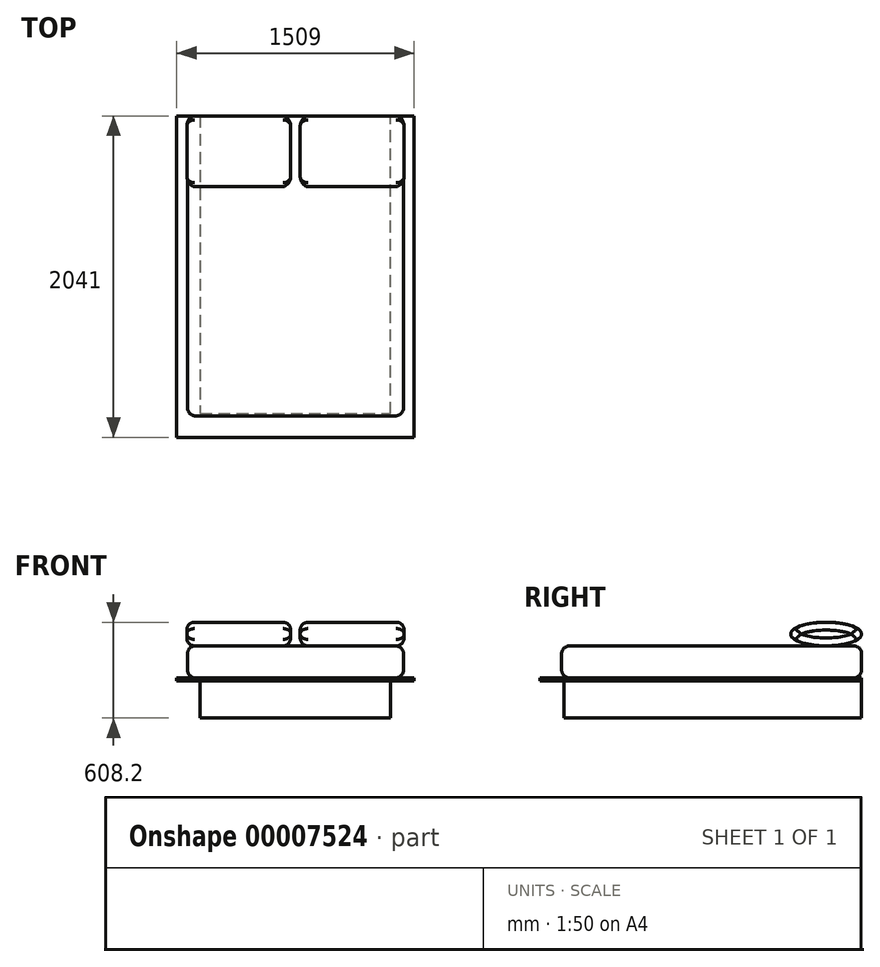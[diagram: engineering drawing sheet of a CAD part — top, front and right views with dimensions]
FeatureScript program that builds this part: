
annotation { "Feature Type Name" : "Feature", "Feature Type Description" : "" }
export const myFeature = defineFeature(function(context is Context, id is Id, definition is map)
    precondition{}
    {
        {
            var Q0;
            Q0=qCreatedBy(makeId("Top.planeOp"),FACE);
            var sketch = newSketch(context, id + "F0", { "sketchPlane" : qUnion([Q0])});
            skLineSegment(sketch, "E0", {"start": v(0, 1020.5) * mm, "end": v(0, -1020.5) * mm, "construction": true});
            skLineSegment(sketch, "E1", {"start": v(-754.5, 0) * mm, "end": v(754.5, 0) * mm, "construction": true});
            skLineSegment(sketch, "E2.bottom", {"start": v(-754.5, 1020.5) * mm, "end": v(754.5, 1020.5) * mm});
            skLineSegment(sketch, "E2.top", {"start": v(-754.5, -1020.5) * mm, "end": v(754.5, -1020.5) * mm});
            skLineSegment(sketch, "E2.left", {"start": v(-754.5, 1020.5) * mm, "end": v(-754.5, -1020.5) * mm});
            skLineSegment(sketch, "E2.right", {"start": v(754.5, 1020.5) * mm, "end": v(754.5, -1020.5) * mm});
            skSolve(sketch);
        }
        {
            var Q0;
            Q0=makeQuery(id+"F0.imprint","IMPRINT",FACE,{"disambiguationData":[TD([[makeQuery(id+"F0.imprint","IMPRINT",EDGE,{"derivedFrom":sQuery(id+"F0.wireOp",EDGE,"E2.bottom")}),-1.0]])]});
            extrude(context, id + "F1", {"entities" : qUnion([Q0]), "oppositeDirection" : true, "depth" : 19 * mm});
        }
        {
            var Q0;
            Q0=makeQuery(id+"F1.opExtrude","CAP_FACE",FACE,{"disambiguationData":[OSD([sQuery(id+"F0.wireOp",EDGE,"E2.bottom"),sQuery(id+"F0.wireOp",EDGE,"E2.top"),sQuery(id+"F0.wireOp",EDGE,"E2.left"),sQuery(id+"F0.wireOp",EDGE,"E2.right")])],"isStart":true});
            var sketch = newSketch(context, id + "F2", { "sketchPlane" : qUnion([Q0])});
            skLineSegment(sketch, "E3", {"start": v(-604.5, 1020.5) * mm, "end": v(-604.5, -870.5) * mm});
            skLineSegment(sketch, "E4", {"start": v(-604.5, -870.5) * mm, "end": v(604.5, -870.5) * mm});
            skLineSegment(sketch, "E5", {"start": v(604.5, -870.5) * mm, "end": v(604.5, 1020.5) * mm});
            skLineSegment(sketch, "E6", {"start": v(0, 0) * mm, "end": v(0, -870.5) * mm, "construction": true});
            skSolve(sketch);
        }
        {
            var Q0;
            {var subQ2=sQuery(id+"F2.wireOp",EDGE,"E3");Q0=makeQuery(id+"F2.imprint","IMPRINT",FACE,{"disambiguationData":[TD([[makeQuery(id+"F2.imprint","IMPRINT",EDGE,{"derivedFrom":subQ2}),1.0]])]});}
            extrude(context, id + "F3", {"entities" : qUnion([Q0]), "operationType" : NewBodyOperationType.ADD, "oppositeDirection" : true, "depth" : 255 * mm});
        }
        {
            var Q0;
            Q0=makeQuery(id+"F1.opExtrude","CAP_FACE",FACE,{"disambiguationData":[OSD([sQuery(id+"F0.wireOp",EDGE,"E2.bottom"),sQuery(id+"F0.wireOp",EDGE,"E2.top"),sQuery(id+"F0.wireOp",EDGE,"E2.left"),sQuery(id+"F0.wireOp",EDGE,"E2.right")])],"isStart":true});
            var sketch = newSketch(context, id + "F4", { "sketchPlane" : qUnion([Q0])});
            skLineSegment(sketch, "E7.bottom", {"start": v(-685.8, 1020.5) * mm, "end": v(685.8, 1020.5) * mm});
            skLineSegment(sketch, "E7.top", {"start": v(-685.8, -884.5) * mm, "end": v(685.8, -884.5) * mm});
            skLineSegment(sketch, "E7.left", {"start": v(-685.8, 1020.5) * mm, "end": v(-685.8, -884.5) * mm});
            skLineSegment(sketch, "E7.right", {"start": v(685.8, 1020.5) * mm, "end": v(685.8, -884.5) * mm});
            skLineSegment(sketch, "E8", {"start": v(0, 1020.5) * mm, "end": v(0, -884.5) * mm, "construction": true});
            skSolve(sketch);
        }
        {
            var Q0;
            Q0 = qSketchRegion(id + "F4", true);
            extrude(context, id + "F5", {"entities" : qUnion([Q0]), "depth" : 203.2 * mm});
        }
        {
            var Q0;
            Q0=makeQuery(id+"F5.opExtrude","CAP_EDGE",EDGE,{"disambiguationData":[OSD([sQuery(id+"F4.wireOp",EDGE,"E7.top")])],"isStart":false});
            var Q1;
            Q1=makeQuery(id+"F5.opExtrude","CAP_EDGE",EDGE,{"disambiguationData":[OSD([sQuery(id+"F4.wireOp",EDGE,"E7.top")])],"isStart":true});
            var Q2;
            Q2=makeQuery(id+"F5.opExtrude","CAP_EDGE",EDGE,{"disambiguationData":[OSD([sQuery(id+"F4.wireOp",EDGE,"E7.left")])],"isStart":true});
            var Q3;
            Q3=makeQuery(id+"F5.opExtrude","CAP_EDGE",EDGE,{"disambiguationData":[OSD([sQuery(id+"F4.wireOp",EDGE,"E7.left")])],"isStart":false});
            var Q4;
            Q4=makeQuery(id+"F5.opExtrude","SWEPT_EDGE",EDGE,{"disambiguationData":[OSD([sQuery(id+"F4.wireOp",EDGE,"E7.top"),sQuery(id+"F4.wireOp",EDGE,"E7.left")])]});
            var Q5;
            Q5=makeQuery(id+"F5.opExtrude","SWEPT_EDGE",EDGE,{"disambiguationData":[OSD([sQuery(id+"F4.wireOp",EDGE,"E7.top"),sQuery(id+"F4.wireOp",EDGE,"E7.right")])]});
            var Q6;
            Q6=makeQuery(id+"F5.opExtrude","CAP_EDGE",EDGE,{"disambiguationData":[OSD([sQuery(id+"F4.wireOp",EDGE,"E7.right")])],"isStart":false});
            var Q7;
            Q7=makeQuery(id+"F5.opExtrude","CAP_EDGE",EDGE,{"disambiguationData":[OSD([sQuery(id+"F4.wireOp",EDGE,"E7.right")])],"isStart":true});
            var Q8;
            Q8=makeQuery(id+"F5.opExtrude","SWEPT_EDGE",EDGE,{"disambiguationData":[OSD([sQuery(id+"F4.wireOp",EDGE,"E7.bottom"),sQuery(id+"F4.wireOp",EDGE,"E7.right")])]});
            var Q9;
            Q9=makeQuery(id+"F5.opExtrude","CAP_EDGE",EDGE,{"disambiguationData":[OSD([sQuery(id+"F4.wireOp",EDGE,"E7.bottom")])],"isStart":false});
            var Q10;
            Q10=makeQuery(id+"F5.opExtrude","CAP_EDGE",EDGE,{"disambiguationData":[OSD([sQuery(id+"F4.wireOp",EDGE,"E7.bottom")])],"isStart":true});
            var Q11;
            Q11=makeQuery(id+"F5.opExtrude","SWEPT_EDGE",EDGE,{"disambiguationData":[OSD([sQuery(id+"F4.wireOp",EDGE,"E7.bottom"),sQuery(id+"F4.wireOp",EDGE,"E7.left")])]});
            fillet(context, id + "F6", {"entities" : qUnion([Q0, Q1, Q2, Q3, Q4, Q5, Q6, Q7, Q8, Q9, Q10, Q11]), "radius" : 50 * mm, "tangentPropagation" : true, "allowEdgeOverflow" : false});
        }
        {
            var Q0;
            Q0=qCreatedBy(makeId("Right.planeOp"),FACE);
            var sketch = newSketch(context, id + "F7", { "sketchPlane" : qUnion([Q0])});
            skEllipse(sketch, "E9", {"center": v(795.5, 278.2) * mm, "majorRadius": 75 * mm, "minorRadius": 225 * mm, "majorAxis": v(0, -1)});
            skLineSegment(sketch, "E10", {"start": v(795.5, 278.2) * mm, "end": v(1020.5, 278.2) * mm, "construction": true});
            skSolve(sketch);
        }
        {
            var Q0;
            Q0=makeQuery(id+"F7.imprint","IMPRINT",FACE,{"disambiguationData":[TD([[makeQuery(id+"F7.imprint","IMPRINT",EDGE,{"derivedFrom":sQuery(id+"F7.wireOp",EDGE,"E9")}),1.0]])]});
            var Q1;
            Q1=sQuery(id+"F7.wireOp",EDGE,"E9");
            extrude(context, id + "F8", {"entities" : qUnion([Q0]), "surfaceEntities" : qUnion([Q1]), "depth" : 690 * mm, "hasSecondDirection" : true, "secondDirectionOppositeDirection" : false, "secondDirectionDepth" : 30 * mm});
        }
        {
            var Q0;
            Q0 = qSketchRegion(id + "F7", true);
            extrude(context, id + "F9", {"entities" : qUnion([Q0]), "oppositeDirection" : true, "depth" : 690 * mm, "hasSecondDirection" : true, "secondDirectionOppositeDirection" : true, "secondDirectionDepth" : 30 * mm});
        }
        {
            var Q0;
            Q0=makeQuery(id+"F9.opExtrude","CAP_EDGE",EDGE,{"disambiguationData":[OSD([sQuery(id+"F7.wireOp",EDGE,"E9")])],"isStart":false});
            var Q1;
            Q1=makeQuery(id+"F9.opExtrude","CAP_EDGE",EDGE,{"disambiguationData":[OSD([sQuery(id+"F7.wireOp",EDGE,"E9")])],"isStart":true});
            fillet(context, id + "F10", {"entities" : qUnion([Q0, Q1]), "radius" : 50 * mm, "tangentPropagation" : true, "allowEdgeOverflow" : false});
        }
        {
            var Q0;
            Q0=makeQuery(id+"F8.opExtrude","CAP_EDGE",EDGE,{"disambiguationData":[OSD([sQuery(id+"F7.wireOp",EDGE,"E9")])],"isStart":true});
            var Q1;
            Q1=makeQuery(id+"F8.opExtrude","CAP_EDGE",EDGE,{"disambiguationData":[OSD([sQuery(id+"F7.wireOp",EDGE,"E9")])],"isStart":false});
            fillet(context, id + "F11", {"entities" : qUnion([Q0, Q1]), "radius" : 50 * mm, "tangentPropagation" : true, "allowEdgeOverflow" : false});
        }
    });
